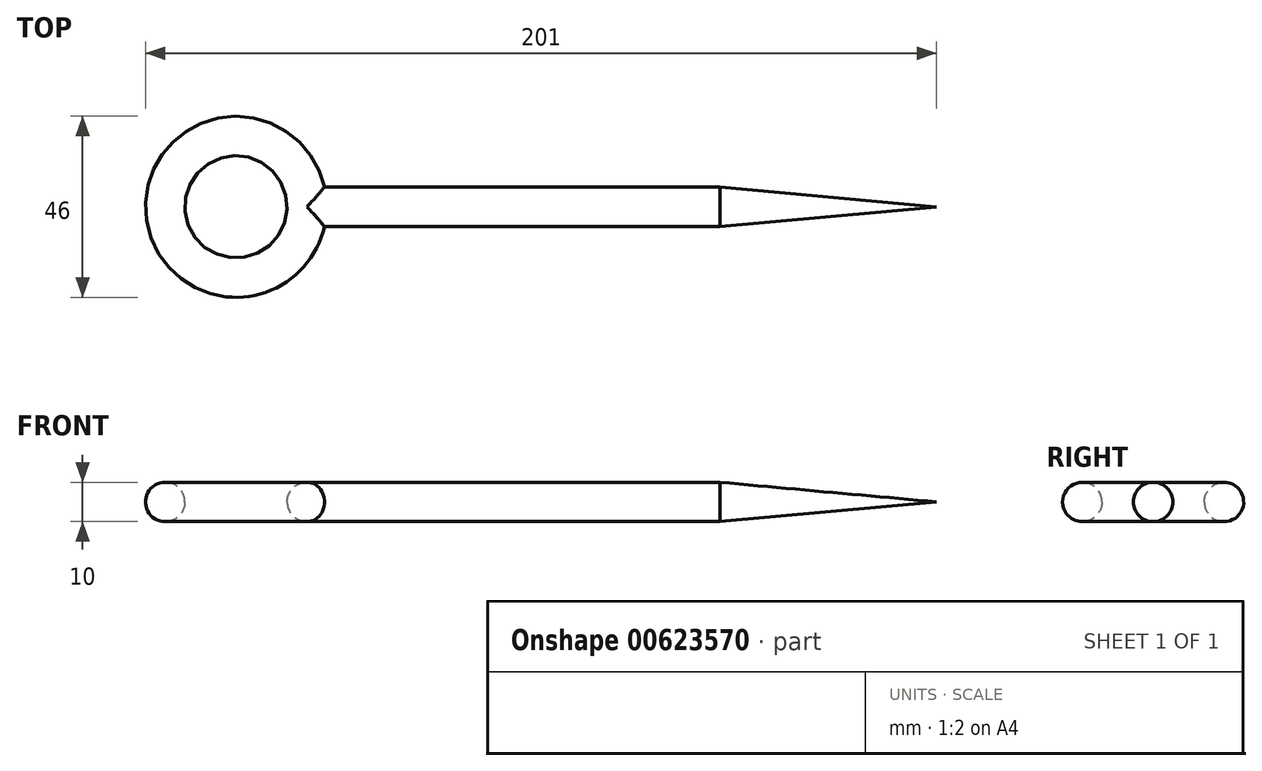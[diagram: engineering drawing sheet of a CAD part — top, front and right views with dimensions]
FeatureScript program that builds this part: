
annotation { "Feature Type Name" : "Feature", "Feature Type Description" : "" }
export const myFeature = defineFeature(function(context is Context, id is Id, definition is map)
    precondition{}
    {
        {
            var Q0;
            Q0=qCreatedBy(makeId("Front.planeOp"),FACE);
            var sketch = newSketch(context, id + "F0", { "sketchPlane" : qUnion([Q0])});
            skCircle(sketch, "E0", {"center": v(18, 0) * mm, "radius": 5 * mm});
            skLineSegment(sketch, "E1", {"start": v(0, 0) * mm, "end": v(0, 51.96) * mm, "construction": true});
            skLineSegment(sketch, "E2", {"start": v(18, 0) * mm, "end": v(18, 5) * mm});
            skLineSegment(sketch, "E3", {"start": v(18, 5) * mm, "end": v(123, 5) * mm});
            skLineSegment(sketch, "E4", {"start": v(123, 5) * mm, "end": v(178, 0) * mm});
            skLineSegment(sketch, "E5", {"start": v(178, 0) * mm, "end": v(18, 0) * mm});
            skPoint(sketch, "E6", {"position": v(123, 0) * mm});
            skSolve(sketch);
        }
        {
            var Q0;
            {var subQ0=sQuery(id+"F0.wireOp",EDGE,"E2");Q0=makeQuery(id+"F0.imprint","IMPRINT",FACE,{"disambiguationData":[TD([[makeQuery(id+"F0.imprint","IMPRINT",EDGE,{"derivedFrom":subQ0}),1.0]])]});}
            var Q1;
            {var subQ0=sQuery(id+"F0.wireOp",EDGE,"E2");Q1=makeQuery(id+"F0.imprint","IMPRINT",FACE,{"disambiguationData":[TD([[makeQuery(id+"F0.imprint","IMPRINT",EDGE,{"derivedFrom":subQ0}),-1.0]])]});}
            var Q2;
            Q2=sQuery(id+"F0.wireOp",EDGE,"E1");
            revolve(context, id + "F1", {"entities" : qUnion([Q0, Q1]), "axis" : qUnion([Q2]), "revolveType" : RevolveType.FULL});
        }
        {
            var Q0;
            {var subQ0=sQuery(id+"F0.wireOp",EDGE,"E3");Q0=makeQuery(id+"F0.imprint","IMPRINT",FACE,{"disambiguationData":[TD([[makeQuery(id+"F0.imprint","IMPRINT",EDGE,{"derivedFrom":subQ0}),-1.0]])]});}
            var Q1;
            {var subQ0=sQuery(id+"F0.wireOp",EDGE,"E2");Q1=makeQuery(id+"F0.imprint","IMPRINT",FACE,{"disambiguationData":[TD([[makeQuery(id+"F0.imprint","IMPRINT",EDGE,{"derivedFrom":subQ0}),-1.0]])]});}
            var Q2;
            Q2=sQuery(id+"F0.wireOp",EDGE,"E5");
            revolve(context, id + "F2", {"operationType" : NewBodyOperationType.ADD, "entities" : qUnion([Q0, Q1]), "axis" : qUnion([Q2]), "revolveType" : RevolveType.FULL});
        }
    });
